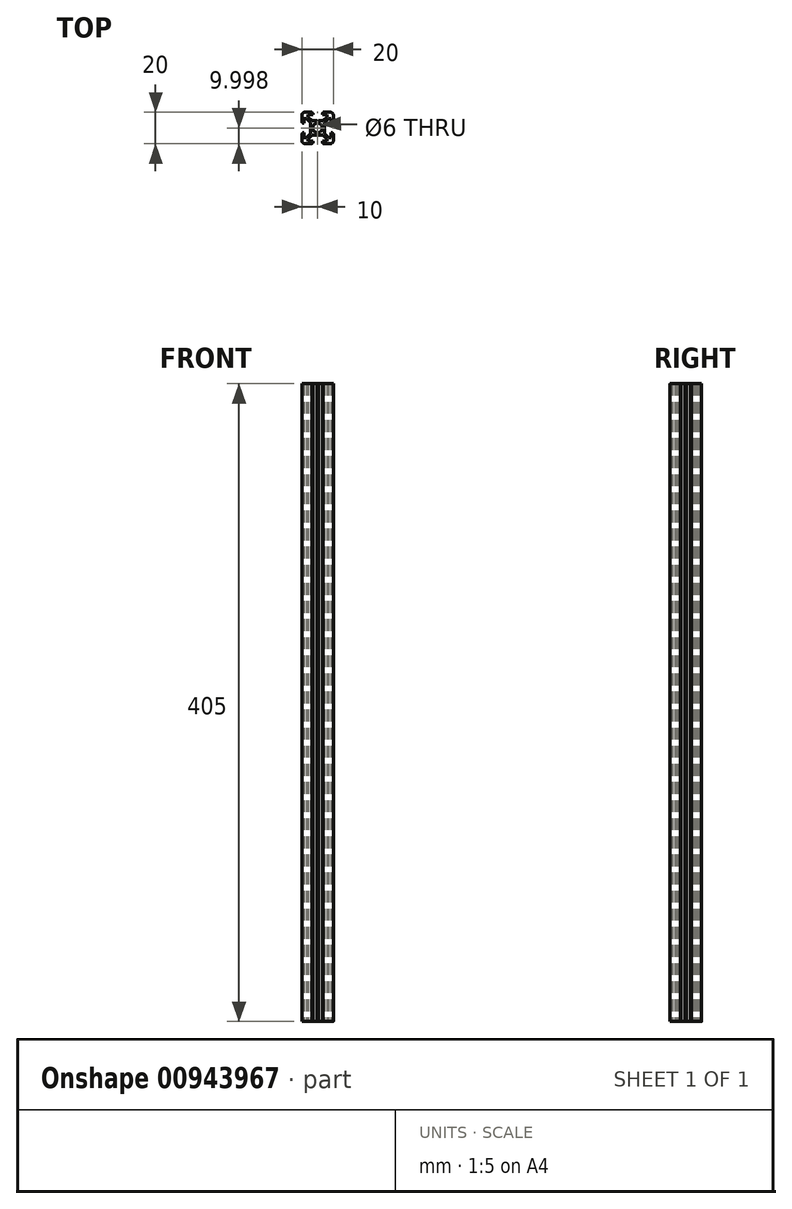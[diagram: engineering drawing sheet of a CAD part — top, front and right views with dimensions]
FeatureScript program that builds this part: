
annotation { "Feature Type Name" : "Feature", "Feature Type Description" : "" }
export const myFeature = defineFeature(function(context is Context, id is Id, definition is map)
    precondition{}
    {
        {
            var Q0;
            Q0=qCreatedBy(makeId("Top.planeOp"),FACE);
            var sketch = newSketch(context, id + "F0", { "sketchPlane" : qUnion([Q0])});
            skLineSegment(sketch, "E0.bottom", {"start": v(-8, -10) * mm, "end": v(8, -10) * mm});
            skLineSegment(sketch, "E0.top", {"start": v(-8, 10) * mm, "end": v(8, 10) * mm});
            skLineSegment(sketch, "E0.left", {"start": v(-10, -8) * mm, "end": v(-10, 8) * mm});
            skLineSegment(sketch, "E0.right", {"start": v(10, -8) * mm, "end": v(10, 8) * mm});
            skPoint(sketch, "E1.visualSharp", {"position": v(10, 10) * mm});
            skArc(sketch, "E1.filletArc", {"start": v(10, 8) * mm, "mid": v(9.41, 9.42) * mm, "end": v(8, 10) * mm});
            skPoint(sketch, "E2.visualSharp", {"position": v(-10, 10) * mm});
            skArc(sketch, "E2.filletArc", {"start": v(-8, 10) * mm, "mid": v(-9.41, 9.42) * mm, "end": v(-10, 8) * mm});
            skPoint(sketch, "E3.visualSharp", {"position": v(-10, -10) * mm});
            skArc(sketch, "E3.filletArc", {"start": v(-10, -8) * mm, "mid": v(-9.41, -9.4) * mm, "end": v(-8, -10) * mm});
            skPoint(sketch, "E4.visualSharp", {"position": v(10, -10) * mm});
            skArc(sketch, "E4.filletArc", {"start": v(8, -10) * mm, "mid": v(9.41, -9.4) * mm, "end": v(10, -8) * mm});
            skLineSegment(sketch, "E5", {"start": v(-10, -10) * mm, "end": v(10, 10) * mm, "construction": true});
            skLineSegment(sketch, "E6", {"start": v(-10, 10) * mm, "end": v(10, -10) * mm, "construction": true});
            skCircle(sketch, "E7", {"center": v(0, 0) * mm, "radius": 3 * mm});
            skCircle(sketch, "E8", {"center": v(0, 0) * mm, "radius": 2.75 * mm});
            skLineSegment(sketch, "E9.bottom", {"start": v(-2.45, -1.73) * mm, "end": v(-1.74, -2.44) * mm});
            skLineSegment(sketch, "E9.top", {"start": v(1.74, 2.45) * mm, "end": v(2.45, 1.75) * mm});
            skLineSegment(sketch, "E9.left", {"start": v(-2.45, -1.73) * mm, "end": v(1.74, 2.45) * mm});
            skLineSegment(sketch, "E9.right", {"start": v(-1.74, -2.44) * mm, "end": v(2.45, 1.75) * mm});
            skLineSegment(sketch, "E10.bottom", {"start": v(-2.45, 1.75) * mm, "end": v(-1.74, 2.45) * mm});
            skLineSegment(sketch, "E10.top", {"start": v(1.74, -2.44) * mm, "end": v(2.45, -1.73) * mm});
            skLineSegment(sketch, "E10.left", {"start": v(-2.45, 1.75) * mm, "end": v(1.74, -2.44) * mm});
            skLineSegment(sketch, "E10.right", {"start": v(-1.74, 2.45) * mm, "end": v(2.45, -1.73) * mm});
            skLineSegment(sketch, "E11", {"start": v(-3.5, 10) * mm, "end": v(-3.5, 9.5) * mm});
            skLineSegment(sketch, "E12", {"start": v(-3.5, 9.5) * mm, "end": v(-3, 9.5) * mm});
            skLineSegment(sketch, "E13", {"start": v(-3, 9.5) * mm, "end": v(-3, 8.5) * mm});
            skLineSegment(sketch, "E14", {"start": v(-3, 8.5) * mm, "end": v(-6, 8.5) * mm});
            skLineSegment(sketch, "E15", {"start": v(-6, 8.5) * mm, "end": v(-6, 7) * mm});
            skLineSegment(sketch, "E16", {"start": v(-3.5, 4.5) * mm, "end": v(-6, 7) * mm});
            skLineSegment(sketch, "E17", {"start": v(-3.5, 4.5) * mm, "end": v(3.5, 4.5) * mm});
            skLineSegment(sketch, "E18", {"start": v(3.5, 4.5) * mm, "end": v(6, 7) * mm});
            skLineSegment(sketch, "E19", {"start": v(6, 7) * mm, "end": v(6, 8.5) * mm});
            skLineSegment(sketch, "E20", {"start": v(6, 8.5) * mm, "end": v(3, 8.5) * mm});
            skLineSegment(sketch, "E21", {"start": v(3, 8.5) * mm, "end": v(3, 9.5) * mm});
            skLineSegment(sketch, "E22", {"start": v(3, 9.5) * mm, "end": v(3.5, 9.5) * mm});
            skLineSegment(sketch, "E23", {"start": v(3.5, 9.5) * mm, "end": v(3.5, 10) * mm});
            skLineSegment(sketch, "E24", {"start": v(0, 10) * mm, "end": v(0, -11.4) * mm, "construction": true});
            skLineSegment(sketch, "E25.1.0", {"start": v(-8.5, -6) * mm, "end": v(-7, -6) * mm});
            skLineSegment(sketch, "E25.1.1", {"start": v(-8.5, -3) * mm, "end": v(-8.5, -6) * mm});
            skLineSegment(sketch, "E25.1.2", {"start": v(-9.5, -3) * mm, "end": v(-8.5, -3) * mm});
            skLineSegment(sketch, "E25.1.3", {"start": v(-9.5, -3.5) * mm, "end": v(-9.5, -3) * mm});
            skLineSegment(sketch, "E25.1.4", {"start": v(-10, -3.5) * mm, "end": v(-9.5, -3.5) * mm});
            skLineSegment(sketch, "E25.1.5", {"start": v(-4.5, -3.5) * mm, "end": v(-7, -6) * mm});
            skLineSegment(sketch, "E25.1.6", {"start": v(-4.5, -3.5) * mm, "end": v(-4.5, 3.5) * mm});
            skLineSegment(sketch, "E25.1.7", {"start": v(-4.5, 3.5) * mm, "end": v(-7, 6) * mm});
            skLineSegment(sketch, "E25.1.8", {"start": v(-7, 6) * mm, "end": v(-8.5, 6) * mm});
            skLineSegment(sketch, "E25.1.9", {"start": v(-8.5, 6) * mm, "end": v(-8.5, 3) * mm});
            skLineSegment(sketch, "E25.1.10", {"start": v(-8.5, 3) * mm, "end": v(-9.5, 3) * mm});
            skLineSegment(sketch, "E25.1.11", {"start": v(-9.5, 3) * mm, "end": v(-9.5, 3.5) * mm});
            skLineSegment(sketch, "E25.1.12", {"start": v(-9.5, 3.5) * mm, "end": v(-10, 3.5) * mm});
            skLineSegment(sketch, "E25.2.0", {"start": v(6, -8.5) * mm, "end": v(6, -7) * mm});
            skLineSegment(sketch, "E25.2.1", {"start": v(3, -8.5) * mm, "end": v(6, -8.5) * mm});
            skLineSegment(sketch, "E25.2.2", {"start": v(3, -9.5) * mm, "end": v(3, -8.5) * mm});
            skLineSegment(sketch, "E25.2.3", {"start": v(3.5, -9.5) * mm, "end": v(3, -9.5) * mm});
            skLineSegment(sketch, "E25.2.4", {"start": v(3.5, -10) * mm, "end": v(3.5, -9.5) * mm});
            skLineSegment(sketch, "E25.2.5", {"start": v(3.5, -4.5) * mm, "end": v(6, -7) * mm});
            skLineSegment(sketch, "E25.2.6", {"start": v(3.5, -4.5) * mm, "end": v(-3.5, -4.5) * mm});
            skLineSegment(sketch, "E25.2.7", {"start": v(-3.5, -4.5) * mm, "end": v(-6, -7) * mm});
            skLineSegment(sketch, "E25.2.8", {"start": v(-6, -7) * mm, "end": v(-6, -8.5) * mm});
            skLineSegment(sketch, "E25.2.9", {"start": v(-6, -8.5) * mm, "end": v(-3, -8.5) * mm});
            skLineSegment(sketch, "E25.2.10", {"start": v(-3, -8.5) * mm, "end": v(-3, -9.5) * mm});
            skLineSegment(sketch, "E25.2.11", {"start": v(-3, -9.5) * mm, "end": v(-3.5, -9.5) * mm});
            skLineSegment(sketch, "E25.2.12", {"start": v(-3.5, -9.5) * mm, "end": v(-3.5, -10) * mm});
            skLineSegment(sketch, "E25.3.0", {"start": v(8.5, 6) * mm, "end": v(7, 6) * mm});
            skLineSegment(sketch, "E25.3.1", {"start": v(8.5, 3) * mm, "end": v(8.5, 6) * mm});
            skLineSegment(sketch, "E25.3.2", {"start": v(9.5, 3) * mm, "end": v(8.5, 3) * mm});
            skLineSegment(sketch, "E25.3.3", {"start": v(9.5, 3.5) * mm, "end": v(9.5, 3) * mm});
            skLineSegment(sketch, "E25.3.4", {"start": v(10, 3.5) * mm, "end": v(9.5, 3.5) * mm});
            skLineSegment(sketch, "E25.3.5", {"start": v(4.5, 3.5) * mm, "end": v(7, 6) * mm});
            skLineSegment(sketch, "E25.3.6", {"start": v(4.5, 3.5) * mm, "end": v(4.5, -3.5) * mm});
            skLineSegment(sketch, "E25.3.7", {"start": v(4.5, -3.5) * mm, "end": v(7, -6) * mm});
            skLineSegment(sketch, "E25.3.8", {"start": v(7, -6) * mm, "end": v(8.5, -6) * mm});
            skLineSegment(sketch, "E25.3.9", {"start": v(8.5, -6) * mm, "end": v(8.5, -3) * mm});
            skLineSegment(sketch, "E25.3.10", {"start": v(8.5, -3) * mm, "end": v(9.5, -3) * mm});
            skLineSegment(sketch, "E25.3.11", {"start": v(9.5, -3) * mm, "end": v(9.5, -3.5) * mm});
            skLineSegment(sketch, "E25.3.12", {"start": v(9.5, -3.5) * mm, "end": v(10, -3.5) * mm});
            skLineSegment(sketch, "E26", {"start": v(-0.5, 4.5) * mm, "end": v(0, 4) * mm});
            skLineSegment(sketch, "E27", {"start": v(0, 4) * mm, "end": v(0.5, 4.5) * mm});
            skLineSegment(sketch, "E28.1.0", {"start": v(-4, 0) * mm, "end": v(-4.5, 0.5) * mm});
            skLineSegment(sketch, "E28.1.1", {"start": v(-4.5, -0.5) * mm, "end": v(-4, 0) * mm});
            skLineSegment(sketch, "E28.2.0", {"start": v(0, -4) * mm, "end": v(-0.5, -4.5) * mm});
            skLineSegment(sketch, "E28.2.1", {"start": v(0.5, -4.5) * mm, "end": v(0, -4) * mm});
            skLineSegment(sketch, "E28.3.0", {"start": v(4, 0) * mm, "end": v(4.5, -0.5) * mm});
            skLineSegment(sketch, "E28.3.1", {"start": v(4.5, 0.5) * mm, "end": v(4, 0) * mm});
            skSolve(sketch);
        }
        {
            var Q0;
            {var subQ6=sQuery(id+"F0.wireOp",EDGE,"E1.filletArc");Q0=makeQuery(id+"F0.imprint","IMPRINT",FACE,{"disambiguationData":[TD([[makeQuery(id+"F0.imprint","IMPRINT",EDGE,{"derivedFrom":subQ6}),1.0]])]});}
            extrude(context, id + "F1", {"entities" : qUnion([Q0]), "depth" : 405 * mm, "offsetDistance" : 25.4 * mm});
        }
    });
